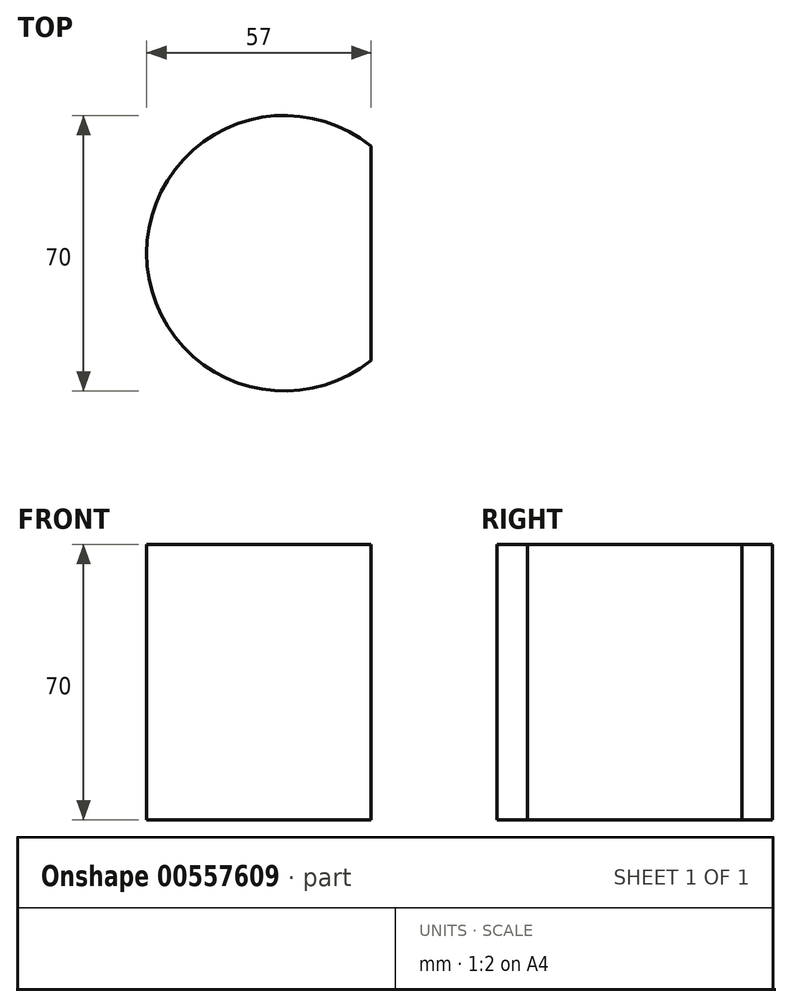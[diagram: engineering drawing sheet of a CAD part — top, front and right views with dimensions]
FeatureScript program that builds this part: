
annotation { "Feature Type Name" : "Feature", "Feature Type Description" : "" }
export const myFeature = defineFeature(function(context is Context, id is Id, definition is map)
    precondition{}
    {
        {
            var Q0;
            Q0=qCreatedBy(makeId("Top.planeOp"),FACE);
            var sketch = newSketch(context, id + "F0", { "sketchPlane" : qUnion([Q0])});
            skArc(sketch, "E0", {"start": v(22, 27.22) * mm, "mid": v(-35, 0) * mm, "end": v(22, -27.22) * mm});
            skLineSegment(sketch, "E1", {"start": v(22, 27.22) * mm, "end": v(22, -27.22) * mm});
            skSolve(sketch);
        }
        {
            var Q0;
            Q0=makeQuery(id+"F0.imprint","IMPRINT",FACE,{"disambiguationData":[TD([[makeQuery(id+"F0.imprint","IMPRINT",EDGE,{"derivedFrom":sQuery(id+"F0.wireOp",EDGE,"E0")}),1.0]])]});
            extrude(context, id + "F1", {"entities" : qUnion([Q0]), "depth" : 70 * mm, "offsetDistance" : 25 * mm});
        }
    });
